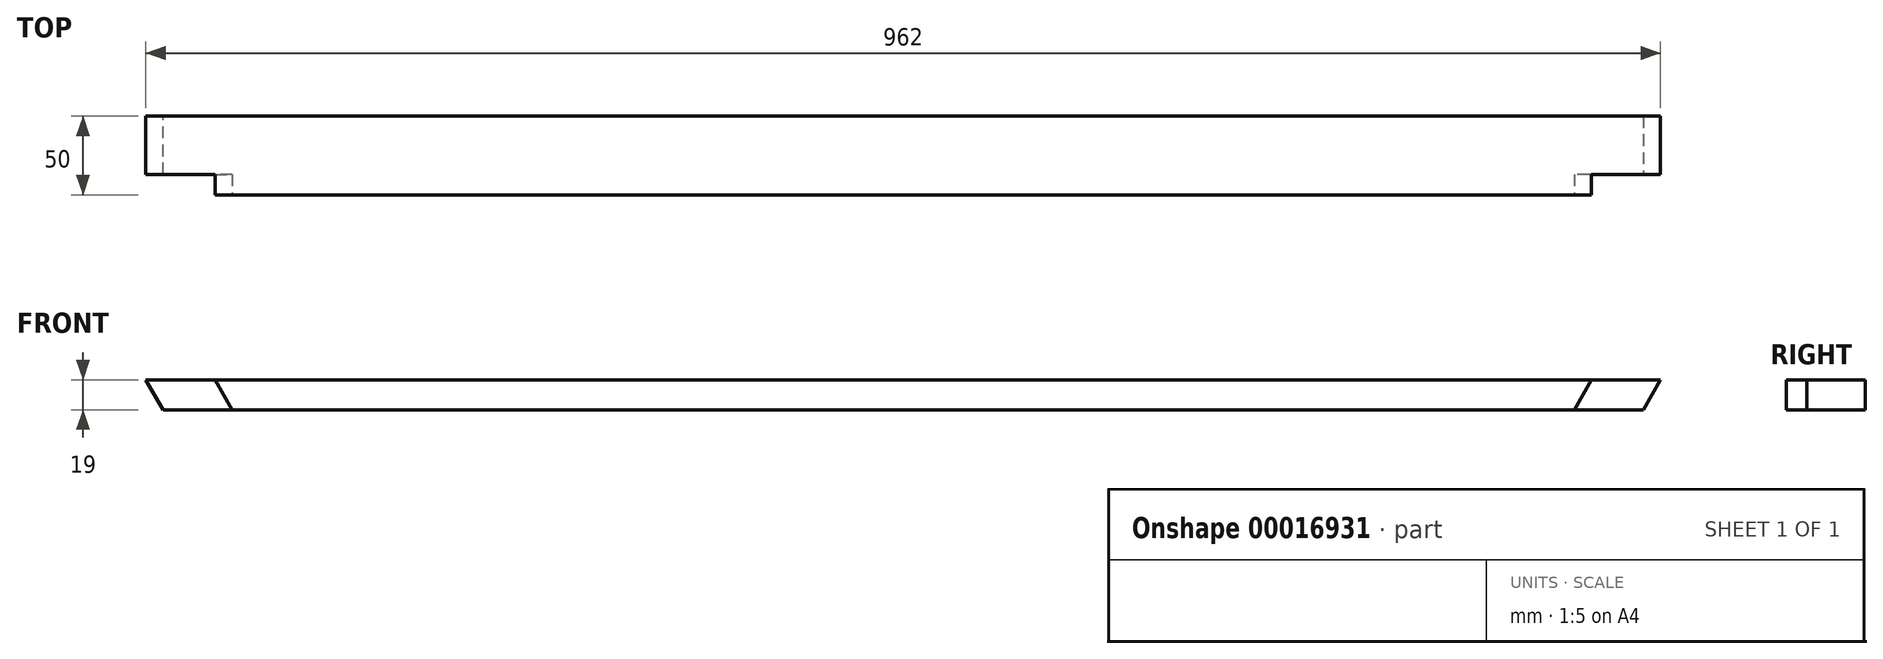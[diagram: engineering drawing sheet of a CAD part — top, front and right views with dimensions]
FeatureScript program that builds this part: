
annotation { "Feature Type Name" : "Feature", "Feature Type Description" : "" }
export const myFeature = defineFeature(function(context is Context, id is Id, definition is map)
    precondition{}
    {
        {
            var Q0;
            Q0=qCreatedBy(makeId("Front.planeOp"),FACE);
            var sketch = newSketch(context, id + "F0", { "sketchPlane" : qUnion([Q0])});
            skLineSegment(sketch, "E0.rect.bottom", {"start": v(481, -9.5) * mm, "end": v(-481, -9.5) * mm});
            skPoint(sketch, "E0.rect.middle", {"position": v(0, 0) * mm});
            skLineSegment(sketch, "E0.rect.top", {"start": v(481, 9.5) * mm, "end": v(-481, 9.5) * mm});
            skLineSegment(sketch, "E0.rect.left", {"start": v(481, -9.5) * mm, "end": v(481, 9.5) * mm});
            skLineSegment(sketch, "E0.rect.right", {"start": v(-481, -9.5) * mm, "end": v(-481, 9.5) * mm});
            skSolve(sketch);
        }
        {
            var Q0;
            Q0 = qSketchRegion(id + "F0", true);
            extrude(context, id + "F1", {"entities" : qUnion([Q0]), "depth" : 50 * mm});
        }
        {
            var Q0;
            Q0=makeQuery(id+"F1.opExtrude","SWEPT_EDGE",EDGE,{"disambiguationData":[OSD([sQuery(id+"F0.wireOp",EDGE,"E0.rect.bottom"),sQuery(id+"F0.wireOp",EDGE,"E0.rect.right")])]});
            var Q1;
            Q1=makeQuery(id+"F1.opExtrude","SWEPT_EDGE",EDGE,{"disambiguationData":[OSD([sQuery(id+"F0.wireOp",EDGE,"E0.rect.bottom"),sQuery(id+"F0.wireOp",EDGE,"E0.rect.left")])]});
            chamfer(context, id + "F2", {"entities" : qUnion([Q0, Q1]), "chamferType" : ChamferType.OFFSET_ANGLE, "width" : 19 * mm, "oppositeDirection" : true, "angle" : 30 * degree, "tangentPropagation" : true});
        }
        {
            var Q0;
            Q0=makeQuery(id+"F1.opExtrude","CAP_FACE",FACE,{"disambiguationData":[OSD([sQuery(id+"F0.wireOp",EDGE,"E0.rect.bottom"),sQuery(id+"F0.wireOp",EDGE,"E0.rect.top"),sQuery(id+"F0.wireOp",EDGE,"E0.rect.left"),sQuery(id+"F0.wireOp",EDGE,"E0.rect.right")])],"isStart":false});
            var sketch = newSketch(context, id + "F3", { "sketchPlane" : qUnion([Q0])});
            skLineSegment(sketch, "E1.0", {"start": v(481, 9.5) * mm, "end": v(470.03, -9.5) * mm});
            skLineSegment(sketch, "E1.1", {"start": v(481, 9.5) * mm, "end": v(437.12, 9.5) * mm});
            skLineSegment(sketch, "E2.0", {"start": v(470.03, -9.5) * mm, "end": v(426.15, -9.5) * mm});
            skLineSegment(sketch, "E3", {"start": v(437.12, 9.5) * mm, "end": v(426.15, -9.5) * mm});
            skLineSegment(sketch, "E4", {"start": v(-437.12, 9.5) * mm, "end": v(-426.15, -9.5) * mm});
            skLineSegment(sketch, "E5.trimOffspring", {"start": v(-481, 9.5) * mm, "end": v(-437.12, 9.5) * mm});
            skLineSegment(sketch, "E6.trimOffspring", {"start": v(-470.03, -9.5) * mm, "end": v(-426.15, -9.5) * mm});
            skSolve(sketch);
        }
        {
            var Q0;
            Q0 = qSketchRegion(id + "F3", true);
            var Q1;
            Q1=makeQuery(id+"F3.imprint","IMPRINT",FACE,{"disambiguationData":[TD([[makeQuery(id+"F3.imprint","IMPRINT",EDGE,{"derivedFrom":sQuery(id+"F3.wireOp",EDGE,"E4")}),-1.0]])]});
            extrude(context, id + "F4", {"entities" : qUnion([Q0, Q1]), "operationType" : NewBodyOperationType.REMOVE, "oppositeDirection" : true, "depth" : 13 * mm});
        }
    });
